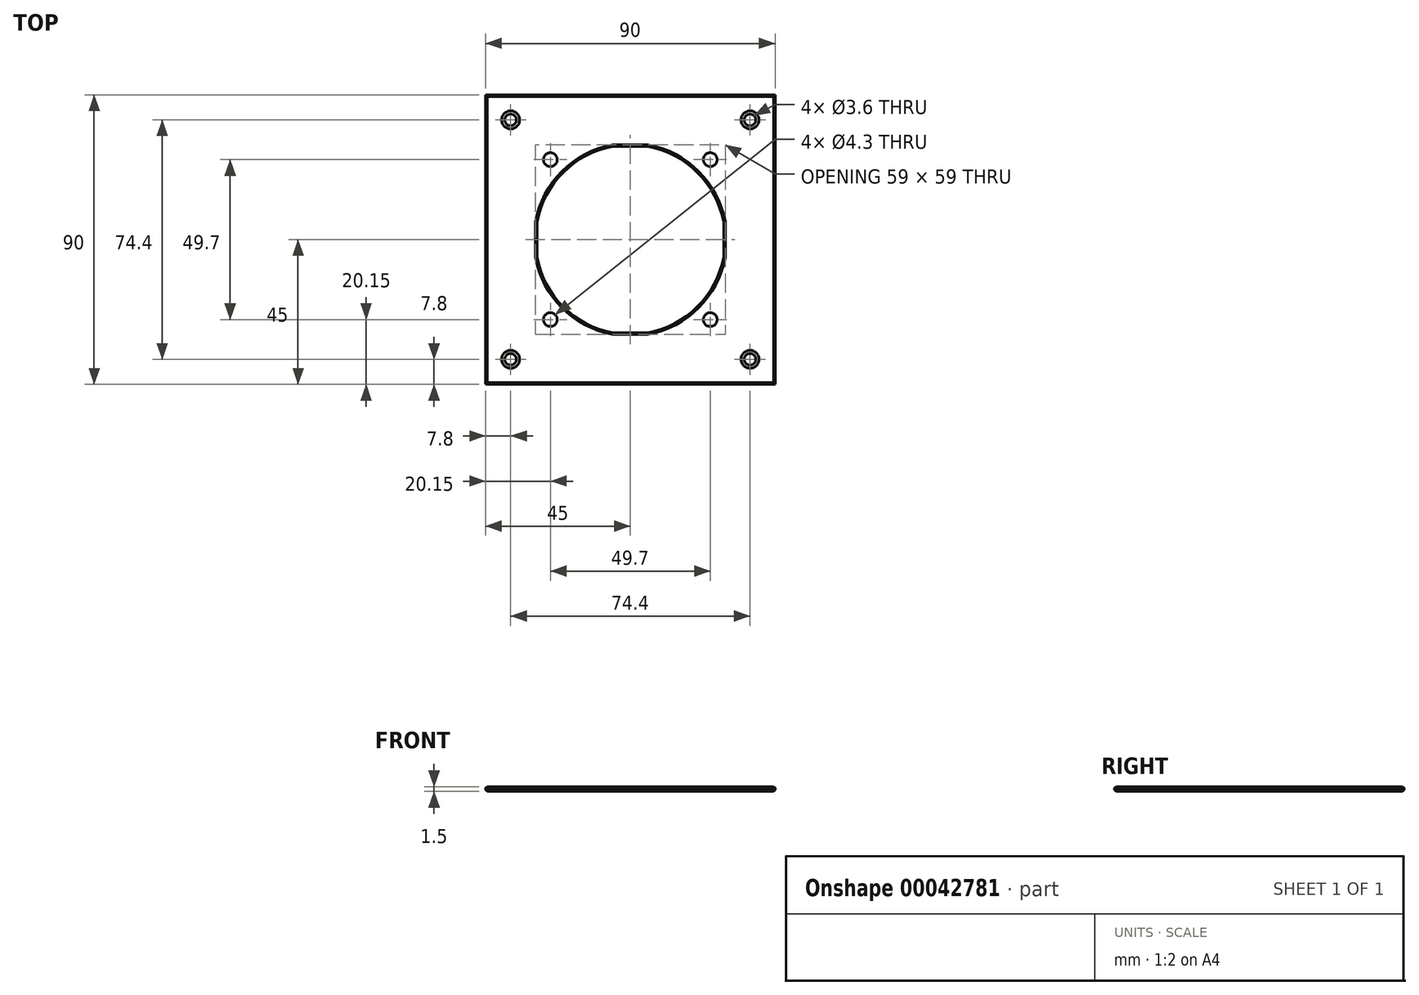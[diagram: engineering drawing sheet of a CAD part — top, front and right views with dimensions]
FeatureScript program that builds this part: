
annotation { "Feature Type Name" : "Feature", "Feature Type Description" : "" }
export const myFeature = defineFeature(function(context is Context, id is Id, definition is map)
    precondition{}
    {
        {
            var Q0;
            Q0=qCreatedBy(makeId("Top.planeOp"),FACE);
            var sketch = newSketch(context, id + "F0", { "sketchPlane" : qUnion([Q0])});
            skLineSegment(sketch, "E0.rect.bottom", {"start": v(30, 30) * mm, "end": v(-30, 30) * mm, "construction": true});
            skLineSegment(sketch, "E0.rect.top", {"start": v(30, -30) * mm, "end": v(-30, -30) * mm, "construction": true});
            skLineSegment(sketch, "E0.rect.left", {"start": v(30, 30) * mm, "end": v(30, -30) * mm, "construction": true});
            skLineSegment(sketch, "E0.rect.right", {"start": v(-30, 30) * mm, "end": v(-30, -30) * mm, "construction": true});
            skPoint(sketch, "E0.rect.middle", {"position": v(0, 0) * mm});
            skLineSegment(sketch, "E1.rect.bottom", {"start": v(45, 45) * mm, "end": v(-45, 45) * mm});
            skLineSegment(sketch, "E1.rect.top", {"start": v(45, -45) * mm, "end": v(-45, -45) * mm});
            skLineSegment(sketch, "E1.rect.left", {"start": v(45, 45) * mm, "end": v(45, -45) * mm});
            skLineSegment(sketch, "E1.rect.right", {"start": v(-45, 45) * mm, "end": v(-45, -45) * mm});
            skLineSegment(sketch, "E2.rect.bottom", {"start": v(5.4, 29) * mm, "end": v(-5.4, 29) * mm});
            skLineSegment(sketch, "E2.rect.top", {"start": v(5.4, -29) * mm, "end": v(-5.4, -29) * mm});
            skLineSegment(sketch, "E2.rect.left", {"start": v(29, 5.4) * mm, "end": v(29, -5.4) * mm});
            skLineSegment(sketch, "E2.rect.right", {"start": v(-29, 5.4) * mm, "end": v(-29, -5.4) * mm});
            skArc(sketch, "E3", {"start": v(-29, -5.4) * mm, "mid": v(-20.86, -20.86) * mm, "end": v(-5.4, -29) * mm});
            skArc(sketch, "E4.trimOffspring", {"start": v(-5.4, 29) * mm, "mid": v(-20.86, 20.86) * mm, "end": v(-29, 5.4) * mm});
            skArc(sketch, "E5.trimOffspring", {"start": v(29, 5.4) * mm, "mid": v(20.86, 20.86) * mm, "end": v(5.4, 29) * mm});
            skArc(sketch, "E6.trimOffspring", {"start": v(5.4, -29) * mm, "mid": v(20.86, -20.86) * mm, "end": v(29, -5.4) * mm});
            skCircle(sketch, "E7", {"center": v(-24.85, 24.85) * mm, "radius": 2.15 * mm});
            skLineSegment(sketch, "E8", {"start": v(-24.85, 27) * mm, "end": v(-24.85, 30) * mm, "construction": true});
            skLineSegment(sketch, "E9", {"start": v(-27, 24.85) * mm, "end": v(-30, 24.85) * mm, "construction": true});
            skCircle(sketch, "E10.MirrorC", {"center": v(24.85, 24.85) * mm, "radius": 2.15 * mm});
            skCircle(sketch, "E11.MirrorC", {"center": v(-24.85, -24.85) * mm, "radius": 2.15 * mm});
            skCircle(sketch, "E12.MirrorC", {"center": v(24.85, -24.85) * mm, "radius": 2.15 * mm});
            skCircle(sketch, "E13", {"center": v(-37.2, 37.2) * mm, "radius": 1.8 * mm});
            skLineSegment(sketch, "E14", {"start": v(-39, 37.2) * mm, "end": v(-45, 37.2) * mm, "construction": true});
            skLineSegment(sketch, "E15", {"start": v(-37.2, 39) * mm, "end": v(-37.2, 45) * mm, "construction": true});
            skCircle(sketch, "E16.MirrorC", {"center": v(37.2, 37.2) * mm, "radius": 1.8 * mm});
            skCircle(sketch, "E17.MirrorC", {"center": v(-37.2, -37.2) * mm, "radius": 1.8 * mm});
            skCircle(sketch, "E18.MirrorC", {"center": v(37.2, -37.2) * mm, "radius": 1.8 * mm});
            skSolve(sketch);
        }
        {
            var Q0;
            Q0=makeQuery(id+"F0.imprint","IMPRINT",FACE,{"disambiguationData":[TD([[makeQuery(id+"F0.imprint","IMPRINT",EDGE,{"derivedFrom":sQuery(id+"F0.wireOp",EDGE,"E1.rect.bottom")}),1.0]])]});
            extrude(context, id + "F1", {"entities" : qUnion([Q0]), "depth" : 1.5 * mm});
        }
        {
            var Q0;
            Q0=makeQuery(id+"F1.opExtrude","CAP_EDGE",EDGE,{"disambiguationData":[OSD([sQuery(id+"F0.wireOp",EDGE,"E13")])],"isStart":false});
            var Q1;
            Q1=makeQuery(id+"F1.opExtrude","CAP_EDGE",EDGE,{"disambiguationData":[OSD([sQuery(id+"F0.wireOp",EDGE,"E16.MirrorC")])],"isStart":false});
            var Q2;
            Q2=makeQuery(id+"F1.opExtrude","CAP_EDGE",EDGE,{"disambiguationData":[OSD([sQuery(id+"F0.wireOp",EDGE,"E18.MirrorC")])],"isStart":false});
            var Q3;
            Q3=makeQuery(id+"F1.opExtrude","CAP_EDGE",EDGE,{"disambiguationData":[OSD([sQuery(id+"F0.wireOp",EDGE,"E17.MirrorC")])],"isStart":false});
            chamfer(context, id + "F2", {"entities" : qUnion([Q0, Q1, Q2, Q3]), "chamferType" : ChamferType.OFFSET_ANGLE, "width" : 1 * mm, "oppositeDirection" : false, "angle" : 45 * degree, "tangentPropagation" : true});
        }
        {
            var Q0;
            Q0=makeQuery(id+"F1.opExtrude","CAP_EDGE",EDGE,{"disambiguationData":[OSD([sQuery(id+"F0.wireOp",EDGE,"E1.rect.top")])],"isStart":true});
            var Q1;
            Q1=makeQuery(id+"F1.opExtrude","CAP_EDGE",EDGE,{"disambiguationData":[OSD([sQuery(id+"F0.wireOp",EDGE,"E1.rect.right")])],"isStart":true});
            var Q2;
            Q2=makeQuery(id+"F1.opExtrude","CAP_EDGE",EDGE,{"disambiguationData":[OSD([sQuery(id+"F0.wireOp",EDGE,"E1.rect.left")])],"isStart":true});
            var Q3;
            Q3=makeQuery(id+"F1.opExtrude","CAP_EDGE",EDGE,{"disambiguationData":[OSD([sQuery(id+"F0.wireOp",EDGE,"E1.rect.bottom")])],"isStart":true});
            var Q4;
            Q4=makeQuery(id+"F1.opExtrude","CAP_EDGE",EDGE,{"disambiguationData":[OSD([sQuery(id+"F0.wireOp",EDGE,"E1.rect.right")])],"isStart":false});
            var Q5;
            Q5=makeQuery(id+"F1.opExtrude","CAP_EDGE",EDGE,{"disambiguationData":[OSD([sQuery(id+"F0.wireOp",EDGE,"E1.rect.top")])],"isStart":false});
            var Q6;
            Q6=makeQuery(id+"F1.opExtrude","CAP_EDGE",EDGE,{"disambiguationData":[OSD([sQuery(id+"F0.wireOp",EDGE,"E1.rect.left")])],"isStart":false});
            var Q7;
            Q7=makeQuery(id+"F1.opExtrude","CAP_EDGE",EDGE,{"disambiguationData":[OSD([sQuery(id+"F0.wireOp",EDGE,"E1.rect.bottom")])],"isStart":false});
            var Q8;
            Q8=makeQuery(id+"F1.opExtrude","CAP_EDGE",EDGE,{"disambiguationData":[OSD([sQuery(id+"F0.wireOp",EDGE,"E3")])],"isStart":true});
            var Q9;
            Q9=makeQuery(id+"F1.opExtrude","CAP_EDGE",EDGE,{"disambiguationData":[OSD([sQuery(id+"F0.wireOp",EDGE,"E3")])],"isStart":false});
            var Q10;
            Q10=makeQuery(id+"F1.opExtrude","CAP_EDGE",EDGE,{"disambiguationData":[OSD([sQuery(id+"F0.wireOp",EDGE,"E2.rect.top")])],"isStart":true});
            var Q11;
            Q11=makeQuery(id+"F1.opExtrude","CAP_EDGE",EDGE,{"disambiguationData":[OSD([sQuery(id+"F0.wireOp",EDGE,"E2.rect.top")])],"isStart":false});
            var Q12;
            Q12=makeQuery(id+"F1.opExtrude","CAP_EDGE",EDGE,{"disambiguationData":[OSD([sQuery(id+"F0.wireOp",EDGE,"E6.trimOffspring")])],"isStart":true});
            var Q13;
            Q13=makeQuery(id+"F1.opExtrude","CAP_EDGE",EDGE,{"disambiguationData":[OSD([sQuery(id+"F0.wireOp",EDGE,"E6.trimOffspring")])],"isStart":false});
            var Q14;
            Q14=makeQuery(id+"F1.opExtrude","CAP_EDGE",EDGE,{"disambiguationData":[OSD([sQuery(id+"F0.wireOp",EDGE,"E2.rect.right")])],"isStart":true});
            var Q15;
            Q15=makeQuery(id+"F1.opExtrude","CAP_EDGE",EDGE,{"disambiguationData":[OSD([sQuery(id+"F0.wireOp",EDGE,"E2.rect.right")])],"isStart":false});
            var Q16;
            Q16=makeQuery(id+"F1.opExtrude","CAP_EDGE",EDGE,{"disambiguationData":[OSD([sQuery(id+"F0.wireOp",EDGE,"E4.trimOffspring")])],"isStart":false});
            var Q17;
            Q17=makeQuery(id+"F1.opExtrude","CAP_EDGE",EDGE,{"disambiguationData":[OSD([sQuery(id+"F0.wireOp",EDGE,"E4.trimOffspring")])],"isStart":true});
            var Q18;
            Q18=makeQuery(id+"F1.opExtrude","CAP_EDGE",EDGE,{"disambiguationData":[OSD([sQuery(id+"F0.wireOp",EDGE,"E5.trimOffspring")])],"isStart":false});
            var Q19;
            Q19=makeQuery(id+"F1.opExtrude","CAP_EDGE",EDGE,{"disambiguationData":[OSD([sQuery(id+"F0.wireOp",EDGE,"E2.rect.left")])],"isStart":false});
            var Q20;
            Q20=makeQuery(id+"F1.opExtrude","CAP_EDGE",EDGE,{"disambiguationData":[OSD([sQuery(id+"F0.wireOp",EDGE,"E2.rect.bottom")])],"isStart":false});
            var Q21;
            Q21=makeQuery(id+"F1.opExtrude","CAP_EDGE",EDGE,{"disambiguationData":[OSD([sQuery(id+"F0.wireOp",EDGE,"E2.rect.left")])],"isStart":true});
            var Q22;
            Q22=makeQuery(id+"F1.opExtrude","CAP_EDGE",EDGE,{"disambiguationData":[OSD([sQuery(id+"F0.wireOp",EDGE,"E5.trimOffspring")])],"isStart":true});
            var Q23;
            Q23=makeQuery(id+"F1.opExtrude","CAP_EDGE",EDGE,{"disambiguationData":[OSD([sQuery(id+"F0.wireOp",EDGE,"E2.rect.bottom")])],"isStart":true});
            chamfer(context, id + "F3", {"entities" : qUnion([Q0, Q1, Q2, Q3, Q4, Q5, Q6, Q7, Q8, Q9, Q10, Q11, Q12, Q13, Q14, Q15, Q16, Q17, Q18, Q19, Q20, Q21, Q22, Q23]), "width" : .5 * mm, "tangentPropagation" : true});
        }
    });
